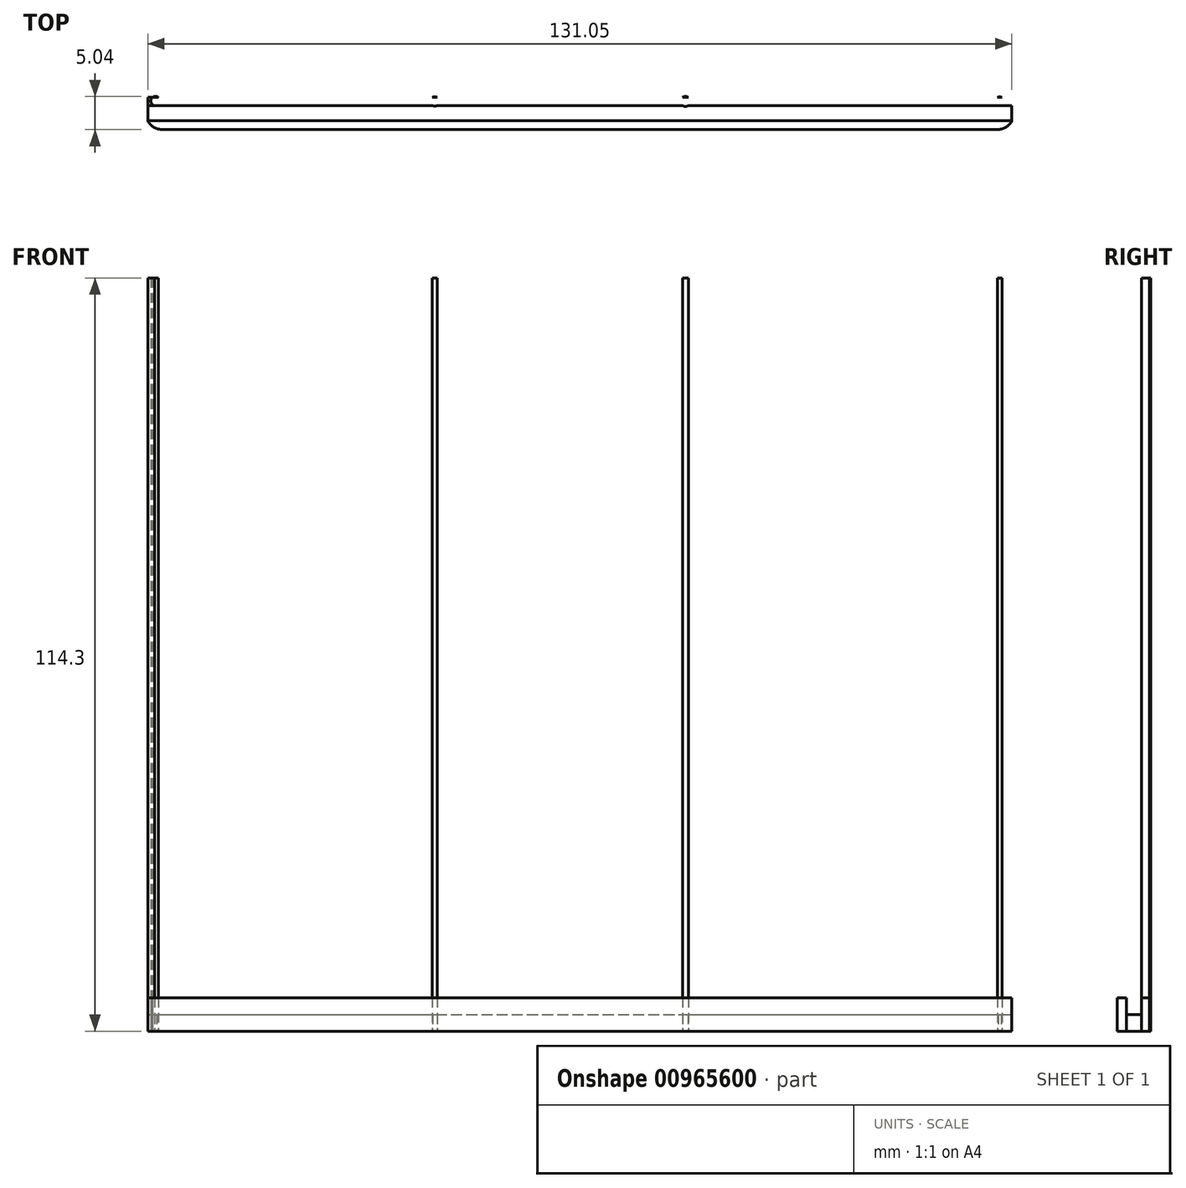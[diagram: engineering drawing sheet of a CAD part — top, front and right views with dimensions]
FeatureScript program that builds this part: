
annotation { "Feature Type Name" : "Feature", "Feature Type Description" : "" }
export const myFeature = defineFeature(function(context is Context, id is Id, definition is map)
    precondition{}
    {
        {
            var Q0;
            Q0=qCreatedBy(makeId("Top.planeOp"),FACE);
            var sketch = newSketch(context, id + "F0", { "sketchPlane" : qUnion([Q0])});
            skLineSegment(sketch, "E0.bottom", {"start": v(-71.17, 22.15) * mm, "end": v(59.88, 22.15) * mm});
            skLineSegment(sketch, "E0.top", {"start": v(-71.17, 17.27) * mm, "end": v(59.88, 17.27) * mm});
            skLineSegment(sketch, "E0.left", {"start": v(-71.17, 22.15) * mm, "end": v(-71.17, 17.27) * mm});
            skLineSegment(sketch, "E0.right", {"start": v(59.88, 22.15) * mm, "end": v(59.88, 17.27) * mm});
            skLineSegment(sketch, "E1", {"start": v(-71.17, 20.92) * mm, "end": v(59.88, 20.92) * mm});
            skLineSegment(sketch, "E2", {"start": v(-71.17, 18.61) * mm, "end": v(59.88, 18.61) * mm});
            skCircle(sketch, "E3", {"center": v(-70, 21.6) * mm, "radius": 0.7 * mm});
            skCircle(sketch, "E4", {"center": v(-27.64, 21.55) * mm, "radius": 0.72 * mm});
            skCircle(sketch, "E5", {"center": v(10.37, 21.55) * mm, "radius": 0.76 * mm});
            skCircle(sketch, "E6", {"center": v(58.02, 21.56) * mm, "radius": 0.68 * mm});
            skSolve(sketch);
        }
        {
            var Q0;
            {var subQ0=sQuery(id+"F0.wireOp",EDGE,"E5");var subQ1=sQuery(id+"F0.wireOp",EDGE,"E0.bottom");var subQ2=makeQuery(id+"F0.imprint","INTERSECT",VERTEX,{"disambiguationData":[OD(0.0)],"derivedFrom":[subQ1,subQ0]});Q0=makeQuery(id+"F0.imprint","IMPRINT",FACE,{"disambiguationData":[TD([[makeQuery(id+"F0.imprint","IMPRINT",EDGE,{"disambiguationData":[TD([[subQ2,1.0]])],"derivedFrom":subQ1}),1.0]])]});}
            var Q1;
            {var subQ0=sQuery(id+"F0.wireOp",EDGE,"E3");var subQ1=sQuery(id+"F0.wireOp",EDGE,"E0.bottom");var subQ2=makeQuery(id+"F0.imprint","INTERSECT",VERTEX,{"disambiguationData":[OD(0.0)],"derivedFrom":[subQ1,subQ0]});Q1=makeQuery(id+"F0.imprint","IMPRINT",FACE,{"disambiguationData":[TD([[makeQuery(id+"F0.imprint","IMPRINT",EDGE,{"disambiguationData":[TD([[subQ2,1.0]])],"derivedFrom":subQ1}),1.0]])]});}
            var Q2;
            {var subQ0=sQuery(id+"F0.wireOp",EDGE,"E4");var subQ1=sQuery(id+"F0.wireOp",EDGE,"E0.bottom");var subQ2=makeQuery(id+"F0.imprint","INTERSECT",VERTEX,{"disambiguationData":[OD(0.0)],"derivedFrom":[subQ1,subQ0]});Q2=makeQuery(id+"F0.imprint","IMPRINT",FACE,{"disambiguationData":[TD([[makeQuery(id+"F0.imprint","IMPRINT",EDGE,{"disambiguationData":[TD([[subQ2,-1.0]])],"derivedFrom":subQ1}),1.0]])]});}
            var Q3;
            {var subQ0=sQuery(id+"F0.wireOp",EDGE,"E6");var subQ1=sQuery(id+"F0.wireOp",EDGE,"E0.bottom");var subQ2=makeQuery(id+"F0.imprint","INTERSECT",VERTEX,{"disambiguationData":[OD(0.0)],"derivedFrom":[subQ1,subQ0]});Q3=makeQuery(id+"F0.imprint","IMPRINT",FACE,{"disambiguationData":[TD([[makeQuery(id+"F0.imprint","IMPRINT",EDGE,{"disambiguationData":[TD([[subQ2,1.0]])],"derivedFrom":subQ1}),1.0]])]});}
            var Q4;
            {var subQ0=sQuery(id+"F0.wireOp",EDGE,"E6");var subQ3=makeQuery(id+"F0.imprint","IMPRINT",VERTEX,{"derivedFrom":subQ0});Q4=makeQuery(id+"F0.imprint","IMPRINT",FACE,{"disambiguationData":[TD([[makeQuery(id+"F0.imprint","IMPRINT",EDGE,{"disambiguationData":[TD([[subQ3,-1.0]])],"derivedFrom":subQ0}),-1.0]])]});}
            var Q5;
            {var subQ0=sQuery(id+"F0.wireOp",EDGE,"E0.left");var subQ1=sQuery(id+"F0.wireOp",EDGE,"E0.bottom");var subQ2=makeQuery(id+"F0.imprint","INTERSECT",VERTEX,{"derivedFrom":[subQ1,subQ0]});Q5=makeQuery(id+"F0.imprint","IMPRINT",FACE,{"disambiguationData":[TD([[makeQuery(id+"F0.imprint","IMPRINT",EDGE,{"disambiguationData":[TD([[subQ2,-1.0]])],"derivedFrom":subQ1}),-1.0]])]});}
            var Q6;
            {var subQ0=sQuery(id+"F0.wireOp",EDGE,"E5");var subQ6=makeQuery(id+"F0.imprint","IMPRINT",VERTEX,{"derivedFrom":subQ0});Q6=makeQuery(id+"F0.imprint","IMPRINT",FACE,{"disambiguationData":[TD([[makeQuery(id+"F0.imprint","IMPRINT",EDGE,{"disambiguationData":[TD([[subQ6,-1.0]])],"derivedFrom":subQ0}),1.0]])]});}
            var Q7;
            {var subQ0=sQuery(id+"F0.wireOp",EDGE,"E3");var subQ5=makeQuery(id+"F0.imprint","IMPRINT",VERTEX,{"derivedFrom":subQ0});Q7=makeQuery(id+"F0.imprint","IMPRINT",FACE,{"disambiguationData":[TD([[makeQuery(id+"F0.imprint","IMPRINT",EDGE,{"disambiguationData":[TD([[subQ5,-1.0]])],"derivedFrom":subQ0}),1.0]])]});}
            var Q8;
            {var subQ0=sQuery(id+"F0.wireOp",EDGE,"E4");var subQ6=makeQuery(id+"F0.imprint","IMPRINT",VERTEX,{"derivedFrom":subQ0});Q8=makeQuery(id+"F0.imprint","IMPRINT",FACE,{"disambiguationData":[TD([[makeQuery(id+"F0.imprint","IMPRINT",EDGE,{"disambiguationData":[TD([[subQ6,-1.0]])],"derivedFrom":subQ0}),1.0]])]});}
            var Q9;
            {var subQ0=sQuery(id+"F0.wireOp",EDGE,"E6");var subQ3=makeQuery(id+"F0.imprint","IMPRINT",VERTEX,{"derivedFrom":subQ0});Q9=makeQuery(id+"F0.imprint","IMPRINT",FACE,{"disambiguationData":[TD([[makeQuery(id+"F0.imprint","IMPRINT",EDGE,{"disambiguationData":[TD([[subQ3,-1.0]])],"derivedFrom":subQ0}),1.0]])]});}
            extrude(context, id + "F1", {"entities" : qUnion([Q0, Q1, Q2, Q3, Q4, Q5, Q6, Q7, Q8, Q9]), "depth" : 114.3 * mm, "offsetDistance" : 25.4 * mm});
        }
        {
            var Q0;
            {var subQ0=sQuery(id+"F0.wireOp",EDGE,"E3");var subQ3=makeQuery(id+"F0.imprint","IMPRINT",VERTEX,{"derivedFrom":subQ0});Q0=makeQuery(id+"F0.imprint","IMPRINT",FACE,{"disambiguationData":[TD([[makeQuery(id+"F0.imprint","IMPRINT",EDGE,{"disambiguationData":[TD([[subQ3,-1.0]])],"derivedFrom":subQ0}),-1.0]])]});}
            var Q1;
            {var subQ0=sQuery(id+"F0.wireOp",EDGE,"E0.top");Q1=makeQuery(id+"F0.imprint","IMPRINT",FACE,{"disambiguationData":[TD([[makeQuery(id+"F0.imprint","IMPRINT",EDGE,{"derivedFrom":subQ0}),1.0]])]});}
            var Q2;
            {var subQ0=sQuery(id+"F0.wireOp",EDGE,"E4");var subQ1=makeQuery(id+"F0.imprint","IMPRINT",VERTEX,{"derivedFrom":subQ0});Q2=makeQuery(id+"F0.imprint","IMPRINT",FACE,{"disambiguationData":[TD([[makeQuery(id+"F0.imprint","IMPRINT",EDGE,{"disambiguationData":[TD([[subQ1,-1.0]])],"derivedFrom":subQ0}),-1.0]])]});}
            var Q3;
            {var subQ0=sQuery(id+"F0.wireOp",EDGE,"E5");var subQ3=makeQuery(id+"F0.imprint","IMPRINT",VERTEX,{"derivedFrom":subQ0});Q3=makeQuery(id+"F0.imprint","IMPRINT",FACE,{"disambiguationData":[TD([[makeQuery(id+"F0.imprint","IMPRINT",EDGE,{"disambiguationData":[TD([[subQ3,-1.0]])],"derivedFrom":subQ0}),-1.0]])]});}
            var Q4;
            {var subQ0=sQuery(id+"F0.wireOp",EDGE,"E6");var subQ3=makeQuery(id+"F0.imprint","IMPRINT",VERTEX,{"derivedFrom":subQ0});Q4=makeQuery(id+"F0.imprint","IMPRINT",FACE,{"disambiguationData":[TD([[makeQuery(id+"F0.imprint","IMPRINT",EDGE,{"disambiguationData":[TD([[subQ3,-1.0]])],"derivedFrom":subQ0}),-1.0]])]});}
            var Q5;
            {var subQ0=sQuery(id+"F0.wireOp",EDGE,"E0.left");var subQ1=sQuery(id+"F0.wireOp",EDGE,"E0.bottom");var subQ2=makeQuery(id+"F0.imprint","INTERSECT",VERTEX,{"derivedFrom":[subQ1,subQ0]});Q5=makeQuery(id+"F0.imprint","IMPRINT",FACE,{"disambiguationData":[TD([[makeQuery(id+"F0.imprint","IMPRINT",EDGE,{"disambiguationData":[TD([[subQ2,-1.0]])],"derivedFrom":subQ1}),-1.0]])]});}
            extrude(context, id + "F2", {"entities" : qUnion([Q0, Q1, Q2, Q3, Q4, Q5]), "depth" : 5.08 * mm, "offsetDistance" : 25.4 * mm});
        }
        {
            var Q0;
            {var subQ4=sQuery(id+"F0.wireOp",EDGE,"E2");Q0=makeQuery(id+"F0.imprint","IMPRINT",FACE,{"disambiguationData":[TD([[makeQuery(id+"F0.imprint","IMPRINT",EDGE,{"derivedFrom":subQ4}),1.0]])]});}
            extrude(context, id + "F3", {"entities" : qUnion([Q0]), "depth" : 2.54 * mm, "offsetDistance" : 25.4 * mm});
        }
        {
            var Q0;
            Q0=makeQuery(id+"F2.opExtrude","SWEPT_EDGE",EDGE,{"disambiguationData":[OSD([sQuery(id+"F0.wireOp",EDGE,"E0.top"),sQuery(id+"F0.wireOp",EDGE,"E0.left")])]});
            var Q1;
            Q1=makeQuery(id+"F2.opExtrude","SWEPT_EDGE",EDGE,{"disambiguationData":[OSD([sQuery(id+"F0.wireOp",EDGE,"E0.top"),sQuery(id+"F0.wireOp",EDGE,"E0.right")])]});
            fillet(context, id + "F4", {"entities" : qUnion([Q0, Q1]), "tangentPropagation" : true, "radius" : 2.54 * mm, "defaultsChanged" : false, "vertexSettings" : [], "allowEdgeOverflow" : false});
        }
    });
